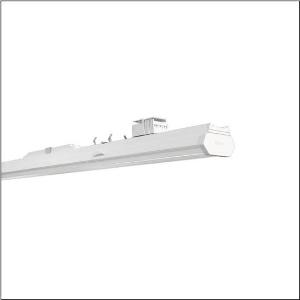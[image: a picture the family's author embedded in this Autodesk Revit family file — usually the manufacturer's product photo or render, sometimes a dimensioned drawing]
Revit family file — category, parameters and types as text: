
# Revit family: licross_r__21_protected_mo_52td11dn48xg_0db0
name_source: partatom
category: Lighting Fixtures
units: mm (PartAtom-declared; Revit-internal decimal feet)

## family parameters
Cut with Voids When Loaded = No
Host = Face
Light Source = No
Part Type = Normal
Room Calculation Point = No
Round Connector Dimension = Use Diameter
Shared = No

## types (1)
- --- (1 x LED, 8000 lm, 45.5 W, 4000K)
    Apparent Load = 46 VA
    CIE Flux Codes = 83 94 98 100 100
    Color Rendering = 80
    Color Temperature = 4000K
    Default Elevation = 1800 mm
    Description = Licross® 21 Protected MO, luminaire insert, of sheet steel, galvanised, coil coated, white, length: 1.500mm, width: 90mm, height: 103mm, LED rated luminous flux: 8.000lm, light colour: 840, control gear: DALI 2, with plug, 5-pole, with phase selection, mains connection: 220..240V, AC, 50/60Hz, rated input power: 46W, halogen-free wiring, primary light control with lens, of plastic, primary optical cover: cover, of PMMA, light emission: direct distribution, primary light characteristic: symmetric, protection rating (complete): IP54, insulation class (complete): insulation class I (protective earthing), certification: CE, ENEC, VDE, UKCA, protection symbol: D if used in an environment with non-conductive dust loads with corresponding accessories, impact resistance: IK06, permissible ambient temperature for indoor applications: -25..+45°C, corresponds to IFS (International Featured Standards) requirements for safety and quality in the food industry, reducing of maximum allowable ambient temperature of 5°C with ceiling mounting, LABS conformity tested according to VDMA 24364:2018-05, packaging unit: 1 piece
    Height = 92 mm
    Lamp = 1 x LED
    Lamp Light Flux = 8000 lm
    Lamp Power = 45.5 W
    Lamp count = 1
    Length = 1500 mm
    Luminous efficacy = 176 lm/W
    Manufacturer = Siteco
    ModVariant = No
    Model = 52TD11DN48XG
    Mounting Place = Ceiling
    Mounting Type = Pendant
    Number of Poles = 1
    OnlyDefault = Yes
    Power Factor = 1
    Product Name = Licross® 21 Protected MO
    Product group = luminaire insert
    ProductGroupID = 901
    Protection Class = Protection class I
    Protection Degree = IP 54
    RLX_Detail_Level = 1
    RLX_Emergency_Light_Flux = 0 lm
    RLX_Emergency_Type = 0
    RLX_Emergency_Type_DB = No
    RlxData = <blob elided: 24077 chars, md5=a022e00a>
    Socket = socket
    Standby Power = 0 W
    System Light Flux = 8000 lm
    System Power = 46 W
    Type Comments = factory setting: luminous flux: 100 % | dim-lin: 254 | 307 mA
    Type Image = l_1256148.jpg
    URL = http://relux.com
    VarID = @adj_098601
    Voltage = 0 V
    Weight = 0.00 kg
    Width = 88 mm

## geometry (parser evidence)
native form markers: Blend x4, Sweep x13
no freeform markers — native parametric forms only
